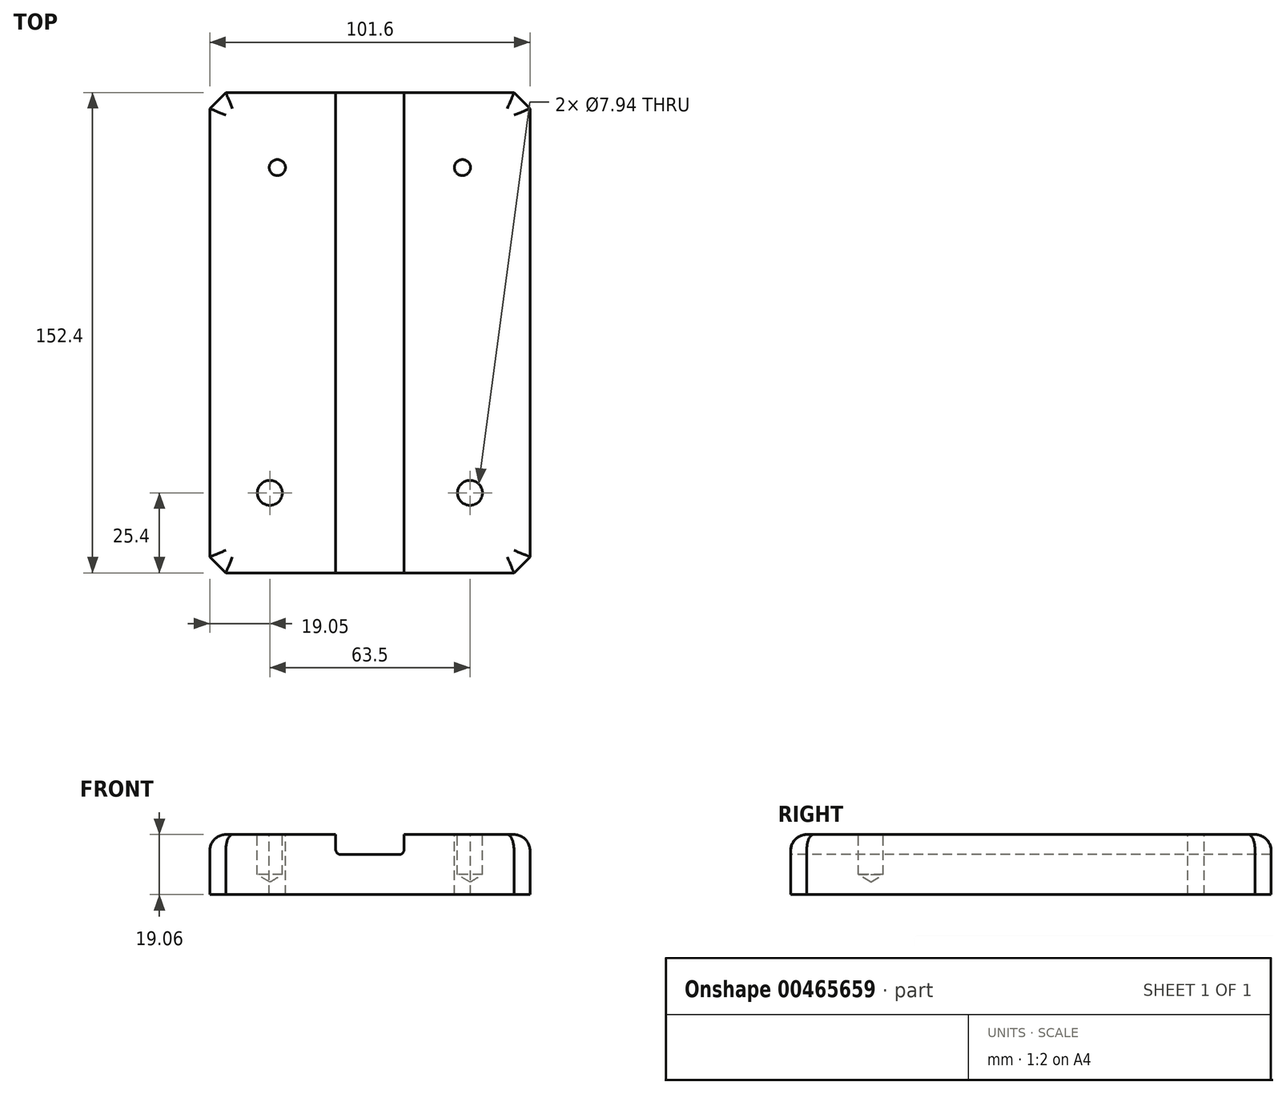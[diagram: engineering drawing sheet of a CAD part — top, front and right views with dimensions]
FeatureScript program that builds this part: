
annotation { "Feature Type Name" : "Feature", "Feature Type Description" : "" }
export const myFeature = defineFeature(function(context is Context, id is Id, definition is map)
    precondition{}
    {
        {
            var Q0;
            Q0=qCreatedBy(makeId("Front.planeOp"),FACE);
            var sketch = newSketch(context, id + "F0", { "sketchPlane" : qUnion([Q0])});
            skLineSegment(sketch, "E0.bottom", {"start": v(-50.8, -9.53) * mm, "end": v(50.8, -9.53) * mm});
            skLineSegment(sketch, "E0.top", {"start": v(-50.8, 9.53) * mm, "end": v(50.8, 9.53) * mm});
            skLineSegment(sketch, "E0.left", {"start": v(-50.8, -9.53) * mm, "end": v(-50.8, 9.53) * mm});
            skLineSegment(sketch, "E0.right", {"start": v(50.8, -9.53) * mm, "end": v(50.8, 9.53) * mm});
            skPoint(sketch, "E0.middle", {"position": v(0, 0) * mm});
            skSolve(sketch);
        }
        {
            var Q0;
            Q0 = qSketchRegion(id + "F0", true);
            extrude(context, id + "F1", {"entities" : qUnion([Q0]), "endBound" : BoundingType.SYMMETRIC, "depth" : 152.4 * mm});
        }
        {
            var Q0;
            Q0=makeQuery(id+"F1.opExtrude","SWEPT_FACE",FACE,{"disambiguationData":[OSD([sQuery(id+"F0.wireOp",EDGE,"E0.top")])]});
            var sketch = newSketch(context, id + "F2", { "sketchPlane" : qUnion([Q0])});
            skPoint(sketch, "E1", {"position": v(-31.75, -50.8) * mm});
            skPoint(sketch, "E2", {"position": v(31.75, -50.8) * mm});
            skSolve(sketch);
        }
        {
            var Q0;
            Q0=sQuery(id+"F2.wireOp",VERTEX,"E1");
            var Q1;
            Q1=sQuery(id+"F2.wireOp",VERTEX,"E2");
            var Q2;
            Q2=makeQuery(id+"F1.opExtrude","SWEPT_BODY",BODY,{"disambiguationData":[OSD([sQuery(id+"F0.wireOp",EDGE,"E0.bottom"),sQuery(id+"F0.wireOp",EDGE,"E0.top"),sQuery(id+"F0.wireOp",EDGE,"E0.left"),sQuery(id+"F0.wireOp",EDGE,"E0.right")])]});
            hole(context, id + "F3", {"style" : HoleStyle.SIMPLE, "endStyle" : HoleEndStyle.BLIND, "standardTappedOrClearance" : lookupTablePath({ "standard" : "ANSI", "engagement" : "75%", "pitch" : "16 tpi", "size" : "3/8", "type" : "Tapped" }), "standardBlindInLast" : lookupTablePath({ "standard" : "ANSI", "engagement" : "75%", "pitch" : "16 tpi", "size" : "3/8", "type" : "Tapped" }), "holeDiameter" : 7.94 * mm, "showTappedDepth" : true, "holeDepth" : 12.7 * mm, "isTappedThrough" : true, "tappedDepth" : 8.9 * mm, "tapClearance" : 16, "startFromSketch" : true, "locations" : qUnion([Q0, Q1]), "scope" : qUnion([Q2]), "majorDiameter" : 9.53 * mm});
        }
        {
            var Q0;
            Q0=makeQuery(id+"F1.opExtrude","CAP_FACE",FACE,{"disambiguationData":[OSD([sQuery(id+"F0.wireOp",EDGE,"E0.bottom"),sQuery(id+"F0.wireOp",EDGE,"E0.top"),sQuery(id+"F0.wireOp",EDGE,"E0.left"),sQuery(id+"F0.wireOp",EDGE,"E0.right")])],"isStart":false});
            var sketch = newSketch(context, id + "F4", { "sketchPlane" : qUnion([Q0])});
            skLineSegment(sketch, "E3.bottom", {"start": v(-10.85, 9.53) * mm, "end": v(10.85, 9.53) * mm});
            skLineSegment(sketch, "E3.top", {"start": v(-9.26, 3.18) * mm, "end": v(9.26, 3.18) * mm});
            skLineSegment(sketch, "E3.left", {"start": v(-10.85, 9.53) * mm, "end": v(-10.85, 4.76) * mm});
            skLineSegment(sketch, "E3.right", {"start": v(10.85, 9.53) * mm, "end": v(10.85, 4.76) * mm});
            skPoint(sketch, "E3.middle", {"position": v(0, 6.35) * mm});
            skPoint(sketch, "E4.visualSharp", {"position": v(-10.85, 3.18) * mm});
            skArc(sketch, "E4.filletArc", {"start": v(-10.85, 4.76) * mm, "mid": v(-10.38, 3.64) * mm, "end": v(-9.26, 3.18) * mm});
            skPoint(sketch, "E5.visualSharp", {"position": v(10.85, 3.18) * mm});
            skArc(sketch, "E5.filletArc", {"start": v(9.26, 3.18) * mm, "mid": v(10.38, 3.64) * mm, "end": v(10.85, 4.76) * mm});
            skSolve(sketch);
        }
        {
            var Q0;
            Q0 = qSketchRegion(id + "F4", true);
            extrude(context, id + "F5", {"entities" : qUnion([Q0]), "operationType" : NewBodyOperationType.REMOVE, "endBound" : BoundingType.THROUGH_ALL, "oppositeDirection" : true, "depth" : 25.4 * mm});
        }
        {
            var Q0;
            {var subQ0=sQuery(id+"F0.wireOp",EDGE,"E0.right");var subQ2=sQuery(id+"F0.wireOp",EDGE,"E0.top");Q0=makeQuery(id+"F5.boolean.opBoolean","SPLIT",FACE,{"disambiguationData":[TD([makeQuery(id+"F1.opExtrude","SWEPT_FACE",FACE,{"disambiguationData":[OSD([subQ0])]})])],"derivedFrom":makeQuery(id+"F1.opExtrude","SWEPT_FACE",FACE,{"disambiguationData":[OSD([subQ2])]})});}
            var sketch = newSketch(context, id + "F6", { "sketchPlane" : qUnion([Q0])});
            skPoint(sketch, "E6", {"position": v(29.36, 52.39) * mm});
            skPoint(sketch, "E7", {"position": v(-29.36, 52.39) * mm});
            skSolve(sketch);
        }
        {
            var Q0;
            Q0=sQuery(id+"F6.wireOp",VERTEX,"E7");
            var Q1;
            Q1=sQuery(id+"F6.wireOp",VERTEX,"E6");
            var Q2;
            Q2=makeQuery(id+"F1.opExtrude","SWEPT_BODY",BODY,{"disambiguationData":[OSD([sQuery(id+"F0.wireOp",EDGE,"E0.bottom"),sQuery(id+"F0.wireOp",EDGE,"E0.top"),sQuery(id+"F0.wireOp",EDGE,"E0.left"),sQuery(id+"F0.wireOp",EDGE,"E0.right")])]});
            hole(context, id + "F7", {"style" : HoleStyle.SIMPLE, "endStyle" : HoleEndStyle.THROUGH, "standardTappedOrClearance" : lookupTablePath({ "standard" : "ANSI", "engagement" : "75%", "pitch" : "20 tpi", "size" : "1/4", "type" : "Tapped" }), "standardBlindInLast" : lookupTablePath({ "standard" : "ANSI", "fit" : "Free", "engagement" : "75%", "pitch" : "20 tpi", "size" : "1/4", "type" : "Clearance & tapped" }), "holeDiameter" : 5.1 * mm, "majorDiameter" : 6.35 * mm, "showTappedDepth" : true, "isTappedThrough" : true, "tappedDepth" : 8.9 * mm, "tapClearance" : 16, "startFromSketch" : true, "locations" : qUnion([Q0, Q1]), "scope" : qUnion([Q2])});
        }
        {
            var Q0;
            Q0=makeQuery(id+"F1.opExtrude","CAP_EDGE",EDGE,{"disambiguationData":[OSD([sQuery(id+"F0.wireOp",EDGE,"E0.right")])],"isStart":true});
            var Q1;
            Q1=makeQuery(id+"F1.opExtrude","CAP_EDGE",EDGE,{"disambiguationData":[OSD([sQuery(id+"F0.wireOp",EDGE,"E0.right")])],"isStart":false});
            var Q2;
            Q2=makeQuery(id+"F1.opExtrude","CAP_EDGE",EDGE,{"disambiguationData":[OSD([sQuery(id+"F0.wireOp",EDGE,"E0.left")])],"isStart":false});
            var Q3;
            Q3=makeQuery(id+"F1.opExtrude","CAP_EDGE",EDGE,{"disambiguationData":[OSD([sQuery(id+"F0.wireOp",EDGE,"E0.left")])],"isStart":true});
            chamfer(context, id + "F8", {"entities" : qUnion([Q0, Q1, Q2, Q3]), "width" : 5.08 * mm, "tangentPropagation" : true});
        }
        {
            var Q0;
            {var subQ0=sQuery(id+"F0.wireOp",EDGE,"E0.left");var subQ2=sQuery(id+"F0.wireOp",EDGE,"E0.top");Q0=makeQuery(id+"F8.opChamfer","BLEND_EDGE",EDGE,{"blendedFrom":[makeQuery(id+"F1.opExtrude","CAP_EDGE",EDGE,{"disambiguationData":[OSD([subQ0])],"isStart":true}),makeQuery(id+"F5.boolean.opBoolean","SPLIT",FACE,{"disambiguationData":[TD([makeQuery(id+"F1.opExtrude","SWEPT_FACE",FACE,{"disambiguationData":[OSD([subQ0])]})])],"derivedFrom":makeQuery(id+"F1.opExtrude","SWEPT_FACE",FACE,{"disambiguationData":[OSD([subQ2])]})})],"blendedInto":[makeQuery(id+"F5.boolean.opBoolean","SPLIT",FACE,{"disambiguationData":[TD([makeQuery(id+"F1.opExtrude","SWEPT_FACE",FACE,{"disambiguationData":[OSD([subQ0])]})])],"derivedFrom":makeQuery(id+"F1.opExtrude","SWEPT_FACE",FACE,{"disambiguationData":[OSD([subQ2])]})})]});}
            var Q1;
            {var subQ0=sQuery(id+"F0.wireOp",EDGE,"E0.left");var subQ1=sQuery(id+"F0.wireOp",EDGE,"E0.top");Q1=makeQuery(id+"F5.boolean.opBoolean","SPLIT",EDGE,{"disambiguationData":[TD([makeQuery(id+"F1.opExtrude","SWEPT_FACE",FACE,{"disambiguationData":[OSD([subQ0])]})])],"derivedFrom":makeQuery(id+"F1.opExtrude","CAP_EDGE",EDGE,{"disambiguationData":[OSD([subQ1])],"isStart":true})});}
            var Q2;
            {var subQ0=sQuery(id+"F0.wireOp",EDGE,"E0.left");var subQ2=sQuery(id+"F0.wireOp",EDGE,"E0.top");Q2=makeQuery(id+"F8.opChamfer","BLEND_EDGE",EDGE,{"blendedFrom":[makeQuery(id+"F1.opExtrude","CAP_EDGE",EDGE,{"disambiguationData":[OSD([subQ0])],"isStart":false}),makeQuery(id+"F5.boolean.opBoolean","SPLIT",FACE,{"disambiguationData":[TD([makeQuery(id+"F1.opExtrude","SWEPT_FACE",FACE,{"disambiguationData":[OSD([subQ0])]})])],"derivedFrom":makeQuery(id+"F1.opExtrude","SWEPT_FACE",FACE,{"disambiguationData":[OSD([subQ2])]})})],"blendedInto":[makeQuery(id+"F5.boolean.opBoolean","SPLIT",FACE,{"disambiguationData":[TD([makeQuery(id+"F1.opExtrude","SWEPT_FACE",FACE,{"disambiguationData":[OSD([subQ0])]})])],"derivedFrom":makeQuery(id+"F1.opExtrude","SWEPT_FACE",FACE,{"disambiguationData":[OSD([subQ2])]})})]});}
            var Q3;
            {var subQ0=sQuery(id+"F0.wireOp",EDGE,"E0.right");var subQ2=sQuery(id+"F0.wireOp",EDGE,"E0.top");Q3=makeQuery(id+"F8.opChamfer","BLEND_EDGE",EDGE,{"blendedFrom":[makeQuery(id+"F1.opExtrude","CAP_EDGE",EDGE,{"disambiguationData":[OSD([subQ0])],"isStart":false}),makeQuery(id+"F5.boolean.opBoolean","SPLIT",FACE,{"disambiguationData":[TD([makeQuery(id+"F1.opExtrude","SWEPT_FACE",FACE,{"disambiguationData":[OSD([subQ0])]})])],"derivedFrom":makeQuery(id+"F1.opExtrude","SWEPT_FACE",FACE,{"disambiguationData":[OSD([subQ2])]})})],"blendedInto":[makeQuery(id+"F5.boolean.opBoolean","SPLIT",FACE,{"disambiguationData":[TD([makeQuery(id+"F1.opExtrude","SWEPT_FACE",FACE,{"disambiguationData":[OSD([subQ0])]})])],"derivedFrom":makeQuery(id+"F1.opExtrude","SWEPT_FACE",FACE,{"disambiguationData":[OSD([subQ2])]})})]});}
            var Q4;
            {var subQ0=sQuery(id+"F0.wireOp",EDGE,"E0.right");var subQ2=sQuery(id+"F0.wireOp",EDGE,"E0.top");Q4=makeQuery(id+"F8.opChamfer","BLEND_EDGE",EDGE,{"blendedFrom":[makeQuery(id+"F1.opExtrude","CAP_EDGE",EDGE,{"disambiguationData":[OSD([subQ0])],"isStart":true}),makeQuery(id+"F5.boolean.opBoolean","SPLIT",FACE,{"disambiguationData":[TD([makeQuery(id+"F1.opExtrude","SWEPT_FACE",FACE,{"disambiguationData":[OSD([subQ0])]})])],"derivedFrom":makeQuery(id+"F1.opExtrude","SWEPT_FACE",FACE,{"disambiguationData":[OSD([subQ2])]})})],"blendedInto":[makeQuery(id+"F5.boolean.opBoolean","SPLIT",FACE,{"disambiguationData":[TD([makeQuery(id+"F1.opExtrude","SWEPT_FACE",FACE,{"disambiguationData":[OSD([subQ0])]})])],"derivedFrom":makeQuery(id+"F1.opExtrude","SWEPT_FACE",FACE,{"disambiguationData":[OSD([subQ2])]})})]});}
            var Q5;
            Q5=makeQuery(id+"F1.opExtrude","SWEPT_EDGE",EDGE,{"disambiguationData":[OSD([sQuery(id+"F0.wireOp",EDGE,"E0.top"),sQuery(id+"F0.wireOp",EDGE,"E0.right")])]});
            var Q6;
            Q6=makeQuery(id+"F1.opExtrude","SWEPT_EDGE",EDGE,{"disambiguationData":[OSD([sQuery(id+"F0.wireOp",EDGE,"E0.top"),sQuery(id+"F0.wireOp",EDGE,"E0.left")])]});
            var Q7;
            {var subQ0=sQuery(id+"F0.wireOp",EDGE,"E0.left");var subQ1=sQuery(id+"F0.wireOp",EDGE,"E0.top");Q7=makeQuery(id+"F5.boolean.opBoolean","SPLIT",EDGE,{"disambiguationData":[TD([makeQuery(id+"F1.opExtrude","SWEPT_FACE",FACE,{"disambiguationData":[OSD([subQ0])]})])],"derivedFrom":makeQuery(id+"F1.opExtrude","CAP_EDGE",EDGE,{"disambiguationData":[OSD([subQ1])],"isStart":false})});}
            var Q8;
            {var subQ0=sQuery(id+"F0.wireOp",EDGE,"E0.right");var subQ1=sQuery(id+"F0.wireOp",EDGE,"E0.top");Q8=makeQuery(id+"F5.boolean.opBoolean","SPLIT",EDGE,{"disambiguationData":[TD([makeQuery(id+"F1.opExtrude","SWEPT_FACE",FACE,{"disambiguationData":[OSD([subQ0])]})])],"derivedFrom":makeQuery(id+"F1.opExtrude","CAP_EDGE",EDGE,{"disambiguationData":[OSD([subQ1])],"isStart":false})});}
            var Q9;
            {var subQ0=sQuery(id+"F0.wireOp",EDGE,"E0.right");var subQ1=sQuery(id+"F0.wireOp",EDGE,"E0.top");Q9=makeQuery(id+"F5.boolean.opBoolean","SPLIT",EDGE,{"disambiguationData":[TD([makeQuery(id+"F1.opExtrude","SWEPT_FACE",FACE,{"disambiguationData":[OSD([subQ0])]})])],"derivedFrom":makeQuery(id+"F1.opExtrude","CAP_EDGE",EDGE,{"disambiguationData":[OSD([subQ1])],"isStart":true})});}
            fillet(context, id + "F9", {"entities" : qUnion([Q0, Q1, Q2, Q3, Q4, Q5, Q6, Q7, Q8, Q9]), "tangentPropagation" : true, "radius" : 5.08 * mm, "defaultsChanged" : false, "vertexSettings" : [], "allowEdgeOverflow" : false});
        }
    });
